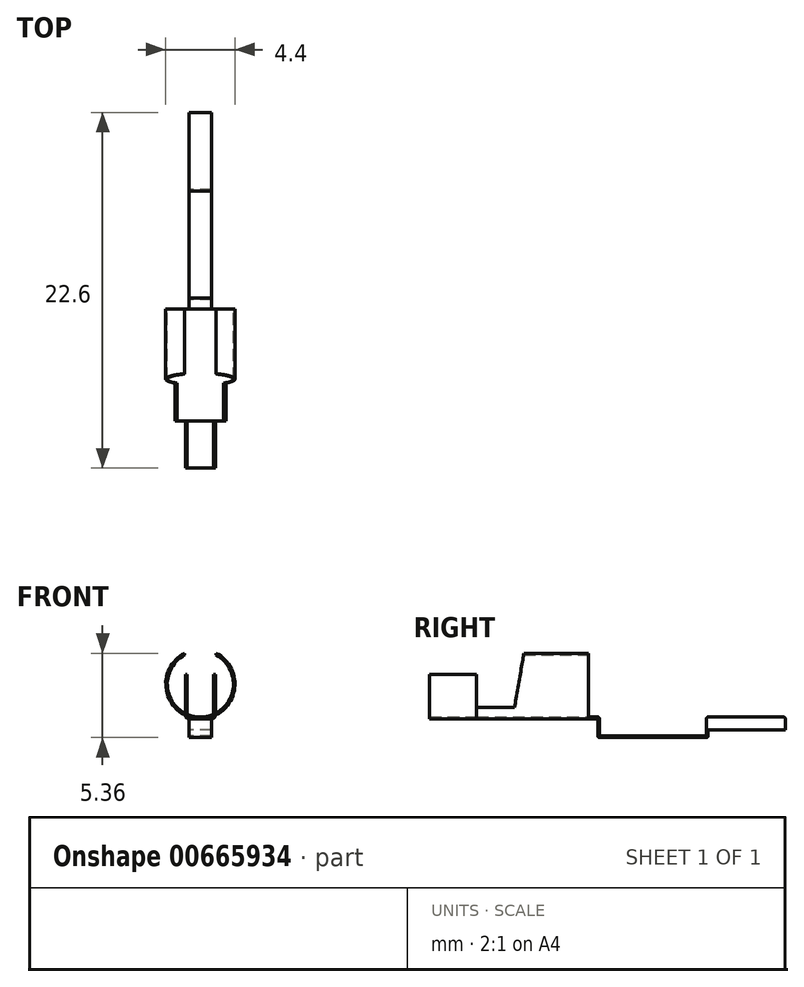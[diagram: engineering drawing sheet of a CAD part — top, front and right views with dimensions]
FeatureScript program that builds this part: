
annotation { "Feature Type Name" : "Feature", "Feature Type Description" : "" }
export const myFeature = defineFeature(function(context is Context, id is Id, definition is map)
    precondition{}
    {
        {
            var Q0;
            Q0=qCreatedBy(makeId("Front.planeOp"),FACE);
            var sketch = newSketch(context, id + "F0", { "sketchPlane" : qUnion([Q0])});
            skArc(sketch, "E0", {"start": v(-1, 1.96) * mm, "mid": v(0, -2.2) * mm, "end": v(1, 1.96) * mm});
            skArc(sketch, "E1", {"start": v(-1, 1.85) * mm, "mid": v(0, -2.1) * mm, "end": v(1, 1.85) * mm});
            skLineSegment(sketch, "E2.left", {"start": v(-1, 1.96) * mm, "end": v(-1, 1.85) * mm});
            skLineSegment(sketch, "E2.right", {"start": v(1, 1.96) * mm, "end": v(1, 1.85) * mm});
            skPoint(sketch, "E2.middle", {"position": v(0, 2.2) * mm});
            skPoint(sketch, "E3.orphan", {"position": v(1, 2.7) * mm});
            skPoint(sketch, "E4.orphan", {"position": v(-1, 1.7) * mm});
            skPoint(sketch, "E5.orphan", {"position": v(-1, 2.7) * mm});
            skPoint(sketch, "E6.orphan", {"position": v(1, 1.7) * mm});
            skSolve(sketch);
        }
        {
            var Q0;
            Q0 = qSketchRegion(id + "F0", true);
            extrude(context, id + "F1", {"entities" : qUnion([Q0]), "depth" : 7.1 * mm, "offsetDistance" : 25 * mm});
        }
        {
            var Q0;
            Q0=makeQuery(id+"F1.opExtrude","CAP_FACE",FACE,{"disambiguationData":[OSD([sQuery(id+"F0.wireOp",EDGE,"E0"),sQuery(id+"F0.wireOp",EDGE,"E1"),sQuery(id+"F0.wireOp",EDGE,"E2.left"),sQuery(id+"F0.wireOp",EDGE,"E2.right")])],"isStart":true});
            var sketch = newSketch(context, id + "F2", { "sketchPlane" : qUnion([Q0])});
            skPoint(sketch, "E7.firstSnap0", {"position": v(0, -2.1) * mm});
            skLineSegment(sketch, "E7.bottom", {"start": v(-0.72, -2.1) * mm, "end": v(0.72, -2.1) * mm});
            skLineSegment(sketch, "E7.top", {"start": v(-0.72, -2.2) * mm, "end": v(0.72, -2.2) * mm});
            skLineSegment(sketch, "E7.left", {"start": v(-0.72, -2.1) * mm, "end": v(-0.72, -2.2) * mm});
            skLineSegment(sketch, "E7.right", {"start": v(0.72, -2.1) * mm, "end": v(0.72, -2.2) * mm});
            skSolve(sketch);
        }
        {
            var Q0;
            Q0 = qSketchRegion(id + "F2", true);
            extrude(context, id + "F3", {"entities" : qUnion([Q0]), "operationType" : NewBodyOperationType.ADD, "depth" : 0.6 * mm, "offsetDistance" : 25 * mm});
        }
        {
            var Q0;
            Q0=makeQuery(id+"F3.opExtrude","SWEPT_FACE",FACE,{"disambiguationData":[OSD([sQuery(id+"F2.wireOp",EDGE,"E7.right")])]});
            var sketch = newSketch(context, id + "F4", { "sketchPlane" : qUnion([Q0])});
            skLineSegment(sketch, "E8.bottom", {"start": v(-0.6, -2.1) * mm, "end": v(-0.7, -2.1) * mm});
            skLineSegment(sketch, "E8.left", {"start": v(-0.6, -2.1) * mm, "end": v(-0.6, -3.4) * mm});
            skLineSegment(sketch, "E8.right", {"start": v(-0.7, -2.1) * mm, "end": v(-0.7, -3.3) * mm});
            skLineSegment(sketch, "E9.bottom", {"start": v(-0.6, -3.4) * mm, "end": v(-7.6, -3.4) * mm});
            skLineSegment(sketch, "E9.top", {"start": v(-0.7, -3.3) * mm, "end": v(-7.5, -3.3) * mm});
            skLineSegment(sketch, "E10.left", {"start": v(-7.6, -3.4) * mm, "end": v(-7.6, -2.9) * mm});
            skLineSegment(sketch, "E10.right", {"start": v(-7.5, -3.3) * mm, "end": v(-7.5, -2.1) * mm});
            skLineSegment(sketch, "E11.bottom", {"start": v(-7.5, -2.1) * mm, "end": v(-12.5, -2.1) * mm});
            skLineSegment(sketch, "E11.top", {"start": v(-7.6, -2.9) * mm, "end": v(-12.5, -2.9) * mm});
            skLineSegment(sketch, "E11.left", {"start": v(-7.5, -2.1) * mm, "end": v(-7.5, -2.9) * mm});
            skLineSegment(sketch, "E11.right", {"start": v(-12.5, -2.1) * mm, "end": v(-12.5, -2.9) * mm});
            skSolve(sketch);
        }
        {
            var Q0;
            Q0 = qSketchRegion(id + "F4", true);
            var Q1;
            Q1=makeQuery(id+"F3.opExtrude","SWEPT_FACE",FACE,{"disambiguationData":[OSD([sQuery(id+"F2.wireOp",EDGE,"E7.left")])]});
            extrude(context, id + "F5", {"entities" : qUnion([Q0]), "operationType" : NewBodyOperationType.ADD, "endBound" : BoundingType.UP_TO_SURFACE, "oppositeDirection" : true, "depth" : 25 * mm, "endBoundEntityFace" : qUnion([Q1]), "offsetDistance" : 25 * mm});
        }
        {
            var Q0;
            Q0=makeQuery(id+"F5.opExtrude","SWEPT_EDGE",EDGE,{"disambiguationData":[OSD([sQuery(id+"F4.wireOp",EDGE,"E8.bottom"),sQuery(id+"F4.wireOp",EDGE,"E8.right")])]});
            var Q1;
            Q1=makeQuery(id+"F3.opExtrude","CAP_EDGE",EDGE,{"disambiguationData":[OSD([sQuery(id+"F2.wireOp",EDGE,"E7.top")])],"isStart":false});
            var Q2;
            Q2=makeQuery(id+"F5.opExtrude","SWEPT_EDGE",EDGE,{"disambiguationData":[OSD([sQuery(id+"F4.wireOp",EDGE,"E8.left"),sQuery(id+"F4.wireOp",EDGE,"E9.bottom")])]});
            var Q3;
            Q3=makeQuery(id+"F5.opExtrude","SWEPT_EDGE",EDGE,{"disambiguationData":[OSD([sQuery(id+"F4.wireOp",EDGE,"E8.right"),sQuery(id+"F4.wireOp",EDGE,"E9.top")])]});
            var Q4;
            Q4=makeQuery(id+"F5.opExtrude","SWEPT_EDGE",EDGE,{"disambiguationData":[OSD([sQuery(id+"F4.wireOp",EDGE,"E9.top"),sQuery(id+"F4.wireOp",EDGE,"E10.right")])]});
            var Q5;
            Q5=makeQuery(id+"F5.opExtrude","SWEPT_EDGE",EDGE,{"disambiguationData":[OSD([sQuery(id+"F4.wireOp",EDGE,"E11.bottom"),sQuery(id+"F4.wireOp",EDGE,"E11.left")])]});
            var Q6;
            Q6=makeQuery(id+"F5.opExtrude","SWEPT_EDGE",EDGE,{"disambiguationData":[OSD([sQuery(id+"F4.wireOp",EDGE,"E9.bottom"),sQuery(id+"F4.wireOp",EDGE,"E10.left")])]});
            fillet(context, id + "F6", {"entities" : qUnion([Q0, Q1, Q2, Q3, Q4, Q5, Q6]), "radius" : 0.1 * mm, "tangentPropagation" : true, "allowEdgeOverflow" : false});
        }
        {
            var Q0;
            Q0=qCreatedBy(makeId("Right.planeOp"),FACE);
            var sketch = newSketch(context, id + "F7", { "sketchPlane" : qUnion([Q0])});
            skLineSegment(sketch, "E12", {"start": v(-4.1, 1.96) * mm, "end": v(-4.7, -1.5) * mm});
            skLineSegment(sketch, "E13.0", {"start": v(-7.1, 1.96) * mm, "end": v(-7.1, -2.2) * mm});
            skLineSegment(sketch, "E14", {"start": v(-4.7, -1.5) * mm, "end": v(-7.1, -1.5) * mm});
            skLineSegment(sketch, "E15", {"start": v(-7.1, 1.96) * mm, "end": v(-4.1, 1.96) * mm});
            skSolve(sketch);
        }
        {
            var Q0;
            Q0 = qSketchRegion(id + "F7", true);
            extrude(context, id + "F8", {"entities" : qUnion([Q0]), "operationType" : NewBodyOperationType.REMOVE, "endBound" : BoundingType.SYMMETRIC, "oppositeDirection" : true, "depth" : 80 * mm, "offsetDistance" : 25 * mm});
        }
        {
            var Q0;
            Q0=makeQuery(id+"F1.opExtrude","CAP_FACE",FACE,{"disambiguationData":[OSD([sQuery(id+"F0.wireOp",EDGE,"E0"),sQuery(id+"F0.wireOp",EDGE,"E1"),sQuery(id+"F0.wireOp",EDGE,"E2.left"),sQuery(id+"F0.wireOp",EDGE,"E2.right")])],"isStart":false});
            var sketch = newSketch(context, id + "F9", { "sketchPlane" : qUnion([Q0])});
            skPoint(sketch, "E16.firstSnap0", {"position": v(0, -2.2) * mm});
            skLineSegment(sketch, "E16.bottom", {"start": v(-0.95, -2.2) * mm, "end": v(0.95, -2.2) * mm});
            skLineSegment(sketch, "E16.top", {"start": v(-0.95, 0.6) * mm, "end": v(-0.85, 0.6) * mm});
            skLineSegment(sketch, "E16.left", {"start": v(-0.95, -2.2) * mm, "end": v(-0.95, 0.6) * mm});
            skLineSegment(sketch, "E16.right", {"start": v(0.95, -2.2) * mm, "end": v(0.95, 0.6) * mm});
            skLineSegment(sketch, "E17.0", {"start": v(0.85, -2.1) * mm, "end": v(0.85, 0.6) * mm});
            skLineSegment(sketch, "E18.0", {"start": v(-0.85, -2.1) * mm, "end": v(-0.85, 0.6) * mm});
            skLineSegment(sketch, "E19.0", {"start": v(-0.85, -2.1) * mm, "end": v(0.85, -2.1) * mm});
            skLineSegment(sketch, "E20.trimOffspring", {"start": v(0.85, 0.6) * mm, "end": v(0.95, 0.6) * mm});
            skSolve(sketch);
        }
        {
            var Q0;
            Q0 = qSketchRegion(id + "F9", true);
            extrude(context, id + "F10", {"entities" : qUnion([Q0]), "operationType" : NewBodyOperationType.ADD, "depth" : 3 * mm, "offsetDistance" : 25 * mm});
        }
        {
            var Q0;
            Q0=makeQuery(id+"F10.opExtrude","SWEPT_EDGE",EDGE,{"disambiguationData":[OSD([sQuery(id+"F9.wireOp",EDGE,"E16.bottom"),sQuery(id+"F9.wireOp",EDGE,"E16.left")])]});
            var Q1;
            Q1=makeQuery(id+"F10.opExtrude","SWEPT_EDGE",EDGE,{"disambiguationData":[OSD([sQuery(id+"F9.wireOp",EDGE,"E16.bottom"),sQuery(id+"F9.wireOp",EDGE,"E16.right")])]});
            var Q2;
            Q2=makeQuery(id+"F10.opExtrude","SWEPT_EDGE",EDGE,{"disambiguationData":[OSD([sQuery(id+"F9.wireOp",EDGE,"E18.0"),sQuery(id+"F9.wireOp",EDGE,"E19.0")])]});
            var Q3;
            Q3=makeQuery(id+"F10.opExtrude","SWEPT_EDGE",EDGE,{"disambiguationData":[OSD([sQuery(id+"F9.wireOp",EDGE,"E17.0"),sQuery(id+"F9.wireOp",EDGE,"E19.0")])]});
            fillet(context, id + "F11", {"entities" : qUnion([Q0, Q1, Q2, Q3]), "radius" : 0.2 * mm, "tangentPropagation" : true, "allowEdgeOverflow" : false});
        }
    });
